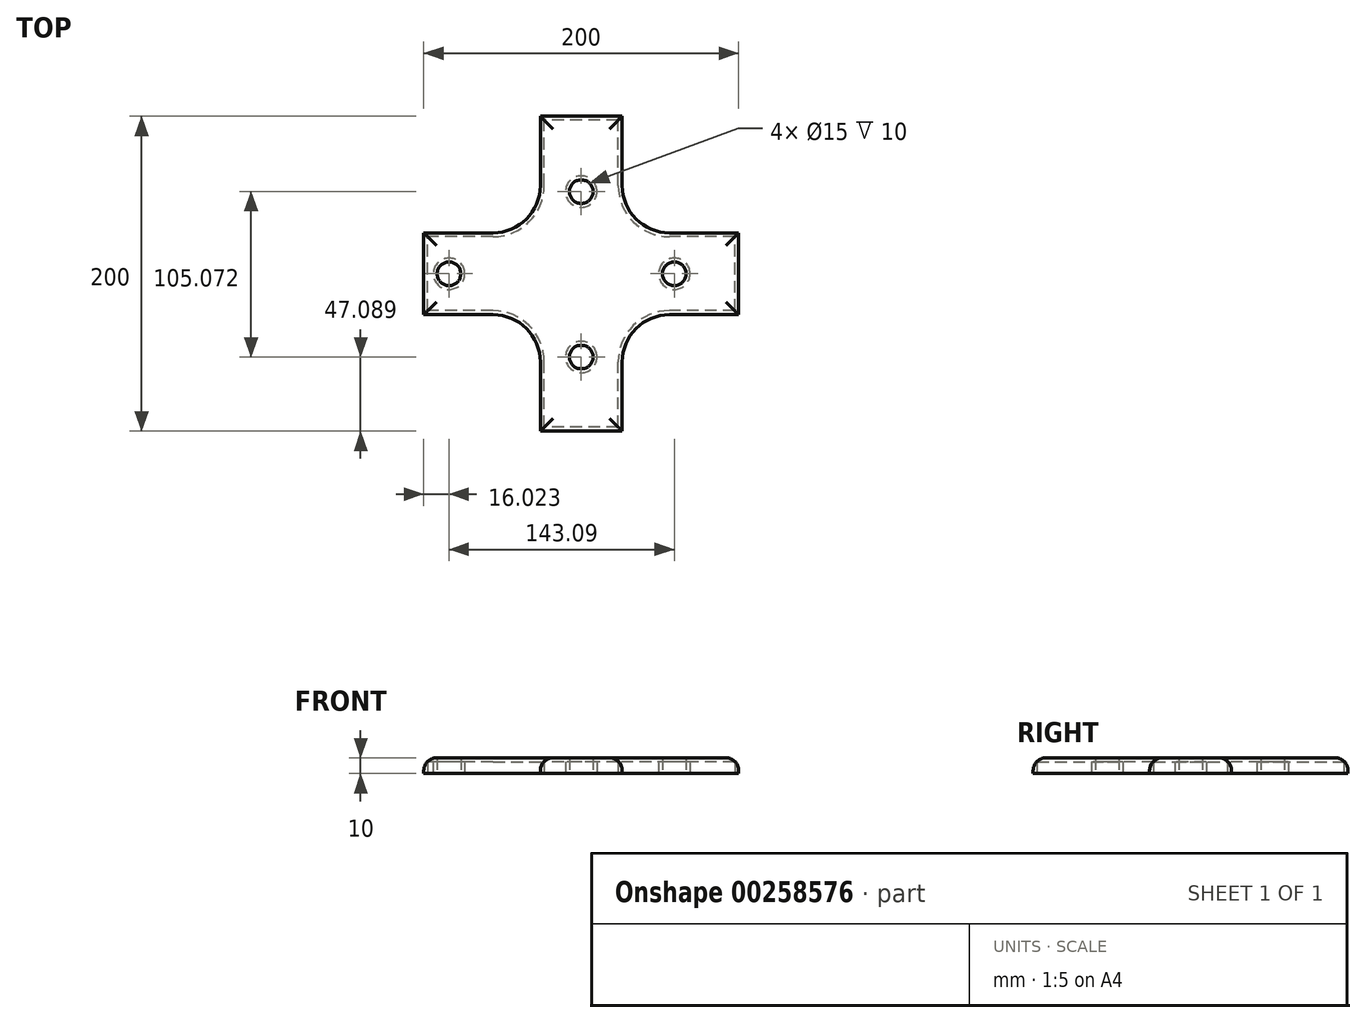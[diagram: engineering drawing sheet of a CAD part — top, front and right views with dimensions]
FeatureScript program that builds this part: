
annotation { "Feature Type Name" : "Feature", "Feature Type Description" : "" }
export const myFeature = defineFeature(function(context is Context, id is Id, definition is map)
    precondition{}
    {
        {
            var Q0;
            Q0=qCreatedBy(makeId("Top.planeOp"),FACE);
            var sketch = newSketch(context, id + "F0", { "sketchPlane" : qUnion([Q0])});
            skLineSegment(sketch, "E0.bottom", {"start": v(26, -100) * mm, "end": v(-26, -100) * mm});
            skLineSegment(sketch, "E0.top", {"start": v(26, 100) * mm, "end": v(-26, 100) * mm});
            skLineSegment(sketch, "E0.left", {"start": v(26, -100) * mm, "end": v(26, 100) * mm});
            skLineSegment(sketch, "E0.right", {"start": v(-26, -100) * mm, "end": v(-26, 100) * mm});
            skPoint(sketch, "E0.middle", {"position": v(0, 0) * mm});
            skLineSegment(sketch, "E1.bottom", {"start": v(100, -26) * mm, "end": v(-100, -26) * mm});
            skLineSegment(sketch, "E1.top", {"start": v(100, 26) * mm, "end": v(-100, 26) * mm});
            skLineSegment(sketch, "E1.left", {"start": v(100, -26) * mm, "end": v(100, 26) * mm});
            skLineSegment(sketch, "E1.right", {"start": v(-100, -26) * mm, "end": v(-100, 26) * mm});
            skPoint(sketch, "E2", {"position": v(26, -26) * mm});
            skPoint(sketch, "E3", {"position": v(26, 26) * mm});
            skPoint(sketch, "E4", {"position": v(-26, 26) * mm});
            skPoint(sketch, "E5", {"position": v(-26, -26) * mm});
            skArc(sketch, "E6", {"start": v(-26, -56) * mm, "mid": v(-34.79, -34.79) * mm, "end": v(-56, -26) * mm});
            skArc(sketch, "E7", {"start": v(26, 56) * mm, "mid": v(34.79, 34.79) * mm, "end": v(56, 26) * mm});
            skArc(sketch, "E8", {"start": v(-56, 26) * mm, "mid": v(-34.79, 34.79) * mm, "end": v(-26, 56) * mm});
            skPoint(sketch, "E9.trimOffspring.end.orphan", {"position": v(26, -56) * mm});
            skPoint(sketch, "E10.start.orphan", {"position": v(56, -26) * mm});
            skArc(sketch, "E11", {"start": v(56, -26) * mm, "mid": v(34.79, -34.79) * mm, "end": v(26, -56) * mm});
            skCircle(sketch, "E12", {"center": v(-83.98, 0) * mm, "radius": 7.5 * mm});
            skPoint(sketch, "E12.centerSnap0", {"position": v(-100, 0) * mm});
            skCircle(sketch, "E13", {"center": v(59.11, 0) * mm, "radius": 7.5 * mm});
            skCircle(sketch, "E14", {"center": v(0, -52.91) * mm, "radius": 7.5 * mm});
            skCircle(sketch, "E15", {"center": v(0, 52.16) * mm, "radius": 7.5 * mm});
            skSolve(sketch);
        }
        {
            var Q0;
            Q0 = qSketchRegion(id + "F0", true);
            var Q1;
            {var subQ0=sQuery(id+"F0.wireOp",EDGE,"E1.bottom");var subQ1=sQuery(id+"F0.wireOp",EDGE,"E0.left");var subQ2=makeQuery(id+"F0.imprint","INTERSECT",VERTEX,{"derivedFrom":[subQ1,subQ0]});Q1=makeQuery(id+"F0.imprint","IMPRINT",FACE,{"disambiguationData":[TD([[makeQuery(id+"F0.imprint","IMPRINT",EDGE,{"disambiguationData":[TD([[subQ2,-1.0]])],"derivedFrom":subQ1}),1.0]])]});}
            extrude(context, id + "F1", {"entities" : qUnion([Q0, Q1]), "depth" : 10 * mm});
        }
        {
            var Q0;
            Q0=makeQuery(id+"F1.opExtrude","CAP_FACE",FACE,{"disambiguationData":[OSD([sQuery(id+"F0.wireOp",EDGE,"E0.bottom"),sQuery(id+"F0.wireOp",EDGE,"E0.top"),sQuery(id+"F0.wireOp",EDGE,"E0.left"),sQuery(id+"F0.wireOp",EDGE,"E0.right"),sQuery(id+"F0.wireOp",EDGE,"E1.bottom"),sQuery(id+"F0.wireOp",EDGE,"E1.top"),sQuery(id+"F0.wireOp",EDGE,"E1.left"),sQuery(id+"F0.wireOp",EDGE,"E1.right"),sQuery(id+"F0.wireOp",EDGE,"E6"),sQuery(id+"F0.wireOp",EDGE,"E7"),sQuery(id+"F0.wireOp",EDGE,"E8"),sQuery(id+"F0.wireOp",EDGE,"E11"),sQuery(id+"F0.wireOp",EDGE,"E12"),sQuery(id+"F0.wireOp",EDGE,"E13"),sQuery(id+"F0.wireOp",EDGE,"E14"),sQuery(id+"F0.wireOp",EDGE,"E15")])],"isStart":true});
            shell(context, id + "F2", {"entities" : qUnion([Q0]), "thickness" : 2.5 * mm});
        }
        {
            var Q0;
            Q0=makeQuery(id+"F1.opExtrude","CAP_EDGE",EDGE,{"disambiguationData":[OSD([sQuery(id+"F0.wireOp",EDGE,"E7")])],"isStart":false});
            var Q1;
            Q1=makeQuery(id+"F1.opExtrude","CAP_EDGE",EDGE,{"disambiguationData":[OSD([sQuery(id+"F0.wireOp",EDGE,"E1.left")])],"isStart":false});
            var Q2;
            {var subQ0=sQuery(id+"F0.wireOp",EDGE,"E1.bottom");Q2=makeQuery(id+"F1.opExtrude","CAP_EDGE",EDGE,{"disambiguationData":[OSD([subQ0]),TDD([makeQuery(id+"F0.imprint","IMPRINT",EDGE,{"disambiguationData":[TD([[makeQuery(id+"F0.imprint","INTERSECT",VERTEX,{"derivedFrom":[subQ0,sQuery(id+"F0.wireOp",EDGE,"E1.left")]}),-1.0]])],"derivedFrom":subQ0})])],"isStart":false});}
            var Q3;
            Q3=makeQuery(id+"F1.opExtrude","CAP_EDGE",EDGE,{"disambiguationData":[OSD([sQuery(id+"F0.wireOp",EDGE,"E11")])],"isStart":false});
            var Q4;
            Q4=makeQuery(id+"F1.opExtrude","CAP_EDGE",EDGE,{"disambiguationData":[OSD([sQuery(id+"F0.wireOp",EDGE,"E0.top")])],"isStart":false});
            var Q5;
            {var subQ0=sQuery(id+"F0.wireOp",EDGE,"E0.right");Q5=makeQuery(id+"F1.opExtrude","CAP_EDGE",EDGE,{"disambiguationData":[OSD([subQ0]),TDD([makeQuery(id+"F0.imprint","IMPRINT",EDGE,{"disambiguationData":[TD([[makeQuery(id+"F0.imprint","INTERSECT",VERTEX,{"derivedFrom":[sQuery(id+"F0.wireOp",EDGE,"E0.top"),subQ0]}),1.0]])],"derivedFrom":subQ0})])],"isStart":false});}
            var Q6;
            Q6=makeQuery(id+"F1.opExtrude","CAP_EDGE",EDGE,{"disambiguationData":[OSD([sQuery(id+"F0.wireOp",EDGE,"E6")])],"isStart":false});
            var Q7;
            Q7=makeQuery(id+"F1.opExtrude","CAP_EDGE",EDGE,{"disambiguationData":[OSD([sQuery(id+"F0.wireOp",EDGE,"E1.right")])],"isStart":false});
            var Q8;
            Q8=makeQuery(id+"F1.opExtrude","CAP_EDGE",EDGE,{"disambiguationData":[OSD([sQuery(id+"F0.wireOp",EDGE,"E0.bottom")])],"isStart":false});
            fillet(context, id + "F3", {"entities" : qUnion([Q0, Q1, Q2, Q3, Q4, Q5, Q6, Q7, Q8]), "radius" : 8 * mm, "tangentPropagation" : true, "allowEdgeOverflow" : false});
        }
    });
